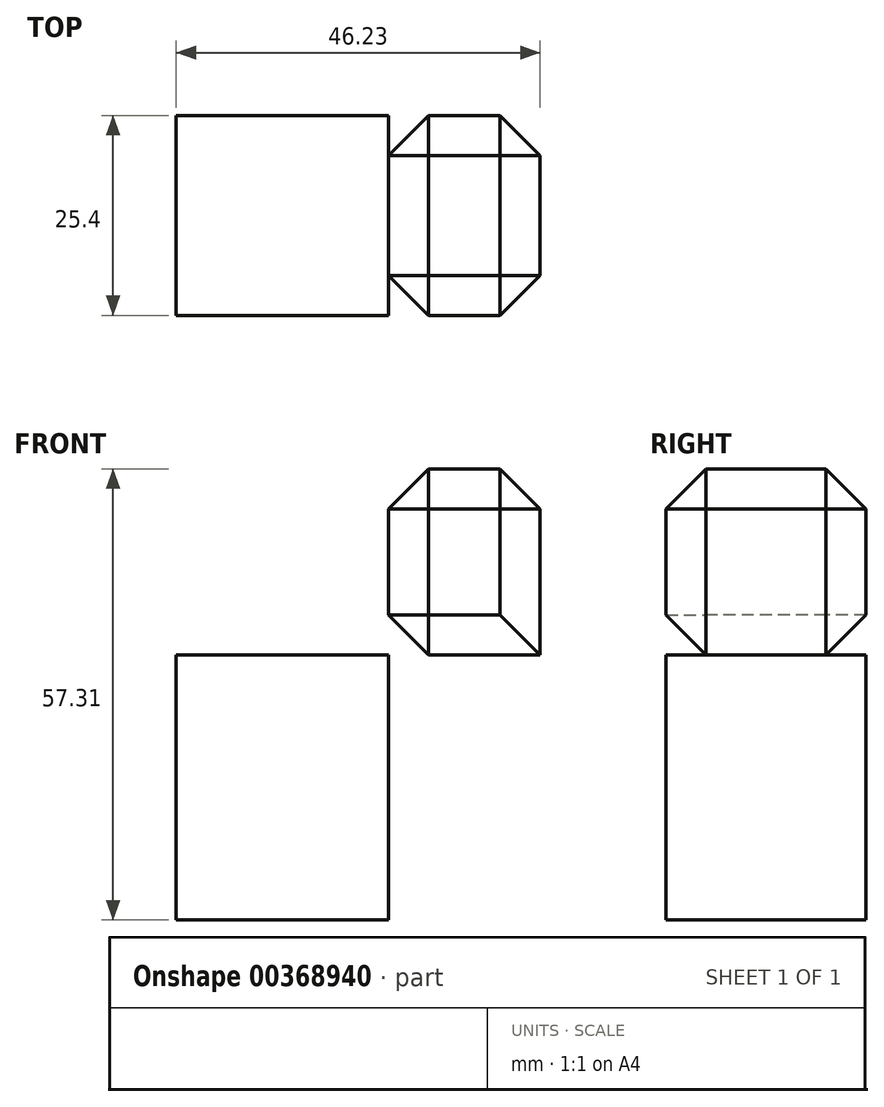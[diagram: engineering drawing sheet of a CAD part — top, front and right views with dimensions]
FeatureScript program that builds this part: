
annotation { "Feature Type Name" : "Feature", "Feature Type Description" : "" }
export const myFeature = defineFeature(function(context is Context, id is Id, definition is map)
    precondition{}
    {
        {
            var Q0;
            Q0=qCreatedBy(makeId("Front.planeOp"),FACE);
            var sketch = newSketch(context, id + "F0", { "sketchPlane" : qUnion([Q0])});
            skLineSegment(sketch, "E0.bottom", {"start": v(27.2, 31.48) * mm, "end": v(10.46, 31.48) * mm});
            skLineSegment(sketch, "E0.top", {"start": v(27.2, 12.24) * mm, "end": v(10.46, 12.24) * mm});
            skLineSegment(sketch, "E0.left", {"start": v(27.2, 31.48) * mm, "end": v(27.2, 12.24) * mm});
            skLineSegment(sketch, "E0.right", {"start": v(10.46, 31.48) * mm, "end": v(10.46, 12.24) * mm});
            skLineSegment(sketch, "E1.bottom", {"start": v(7.95, 7.84) * mm, "end": v(-19.04, 7.84) * mm});
            skLineSegment(sketch, "E1.top", {"start": v(7.95, -25.83) * mm, "end": v(-19.04, -25.83) * mm});
            skLineSegment(sketch, "E1.left", {"start": v(7.95, 7.84) * mm, "end": v(7.95, -25.83) * mm});
            skLineSegment(sketch, "E1.right", {"start": v(-19.04, 7.84) * mm, "end": v(-19.04, -25.83) * mm});
            skLineSegment(sketch, "E2.bottom", {"start": v(-19.04, -25.83) * mm, "end": v(7.95, -25.83) * mm});
            skLineSegment(sketch, "E2.top", {"start": v(-19.04, 7.84) * mm, "end": v(7.95, 7.84) * mm});
            skLineSegment(sketch, "E2.left", {"start": v(-19.04, -25.83) * mm, "end": v(-19.04, 7.84) * mm});
            skLineSegment(sketch, "E2.right", {"start": v(7.95, -25.83) * mm, "end": v(7.95, 7.84) * mm});
            skLineSegment(sketch, "E3.bottom", {"start": v(27.2, 31.48) * mm, "end": v(7.95, 31.48) * mm});
            skLineSegment(sketch, "E3.top", {"start": v(27.2, 7.84) * mm, "end": v(7.95, 7.84) * mm});
            skLineSegment(sketch, "E3.left", {"start": v(27.2, 31.48) * mm, "end": v(27.2, 7.84) * mm});
            skLineSegment(sketch, "E3.right", {"start": v(7.95, 31.48) * mm, "end": v(7.95, 7.84) * mm});
            skSolve(sketch);
        }
        {
            var Q0;
            Q0 = qSketchRegion(id + "F0", true);
            extrude(context, id + "F1", {"entities" : qUnion([Q0]), "depth" : 25.4 * mm});
        }
        {
            var Q0;
            Q0=makeQuery(id+"F1.opExtrude","CAP_EDGE",EDGE,{"disambiguationData":[OSD([sQuery(id+"F0.wireOp",EDGE,"E3.bottom")])],"isStart":true});
            var Q1;
            Q1=makeQuery(id+"F1.opExtrude","SWEPT_FACE",FACE,{"disambiguationData":[OSD([sQuery(id+"F0.wireOp",EDGE,"E3.bottom")])]});
            var Q2;
            Q2=makeQuery(id+"F1.opExtrude","CAP_FACE",FACE,{"disambiguationData":[OSD([sQuery(id+"F0.wireOp",EDGE,"E3.bottom"),sQuery(id+"F0.wireOp",EDGE,"E3.top"),sQuery(id+"F0.wireOp",EDGE,"E3.left"),sQuery(id+"F0.wireOp",EDGE,"E3.right")])],"isStart":true});
            var Q3;
            Q3=makeQuery(id+"F1.opExtrude","CAP_EDGE",EDGE,{"disambiguationData":[OSD([sQuery(id+"F0.wireOp",EDGE,"E3.right")])],"isStart":true});
            var Q4;
            Q4=makeQuery(id+"F1.opExtrude","CAP_EDGE",EDGE,{"disambiguationData":[OSD([sQuery(id+"F0.wireOp",EDGE,"E2.top")])],"isStart":true});
            var Q5;
            Q5=makeQuery(id+"F1.opExtrude","SWEPT_FACE",FACE,{"disambiguationData":[OSD([sQuery(id+"F0.wireOp",EDGE,"E2.left")])]});
            var Q6;
            Q6=makeQuery(id+"F1.opExtrude","CAP_FACE",FACE,{"disambiguationData":[OSD([sQuery(id+"F0.wireOp",EDGE,"E2.bottom"),sQuery(id+"F0.wireOp",EDGE,"E2.top"),sQuery(id+"F0.wireOp",EDGE,"E2.left"),sQuery(id+"F0.wireOp",EDGE,"E2.right")])],"isStart":true});
            var Q7;
            Q7=makeQuery(id+"F1.opExtrude","SWEPT_FACE",FACE,{"disambiguationData":[OSD([sQuery(id+"F0.wireOp",EDGE,"E3.right")])]});
            var Q8;
            Q8=makeQuery(id+"F1.opExtrude","SWEPT_EDGE",EDGE,{"disambiguationData":[OSD([sQuery(id+"F0.wireOp",EDGE,"E3.bottom"),sQuery(id+"F0.wireOp",EDGE,"E3.right")])]});
            var Q9;
            Q9=makeQuery(id+"F1.opExtrude","CAP_FACE",FACE,{"disambiguationData":[OSD([sQuery(id+"F0.wireOp",EDGE,"E3.bottom"),sQuery(id+"F0.wireOp",EDGE,"E3.top"),sQuery(id+"F0.wireOp",EDGE,"E3.left"),sQuery(id+"F0.wireOp",EDGE,"E3.right")])],"isStart":false});
            var Q10;
            Q10=makeQuery(id+"F1.opExtrude","CAP_EDGE",EDGE,{"disambiguationData":[OSD([sQuery(id+"F0.wireOp",EDGE,"E3.right")])],"isStart":false});
            var Q11;
            Q11=makeQuery(id+"F1.opExtrude","CAP_EDGE",EDGE,{"disambiguationData":[OSD([sQuery(id+"F0.wireOp",EDGE,"E2.top")])],"isStart":false});
            var Q12;
            Q12=makeQuery(id+"F1.opExtrude","CAP_EDGE",EDGE,{"disambiguationData":[OSD([sQuery(id+"F0.wireOp",EDGE,"E2.left")])],"isStart":false});
            var Q13;
            Q13=makeQuery(id+"F1.opExtrude","SWEPT_FACE",FACE,{"disambiguationData":[OSD([sQuery(id+"F0.wireOp",EDGE,"E2.top")])]});
            var Q14;
            Q14=makeQuery(id+"F1.opExtrude","CAP_FACE",FACE,{"disambiguationData":[OSD([sQuery(id+"F0.wireOp",EDGE,"E2.bottom"),sQuery(id+"F0.wireOp",EDGE,"E2.top"),sQuery(id+"F0.wireOp",EDGE,"E2.left"),sQuery(id+"F0.wireOp",EDGE,"E2.right")])],"isStart":false});
            var Q15;
            Q15=makeQuery(id+"F1.opExtrude","SWEPT_EDGE",EDGE,{"disambiguationData":[OSD([sQuery(id+"F0.wireOp",EDGE,"E2.top"),sQuery(id+"F0.wireOp",EDGE,"E2.left")])]});
            var Q16;
            Q16=makeQuery(id+"F1.opExtrude","CAP_EDGE",EDGE,{"disambiguationData":[OSD([sQuery(id+"F0.wireOp",EDGE,"E2.left")])],"isStart":true});
            var Q17;
            Q17=makeQuery(id+"F1.opExtrude","CAP_EDGE",EDGE,{"disambiguationData":[OSD([sQuery(id+"F0.wireOp",EDGE,"E2.bottom")])],"isStart":false});
            var Q18;
            Q18=makeQuery(id+"F1.opExtrude","SWEPT_EDGE",EDGE,{"disambiguationData":[OSD([sQuery(id+"F0.wireOp",EDGE,"E2.bottom"),sQuery(id+"F0.wireOp",EDGE,"E2.left")])]});
            var Q19;
            Q19=makeQuery(id+"F1.opExtrude","CAP_EDGE",EDGE,{"disambiguationData":[OSD([sQuery(id+"F0.wireOp",EDGE,"E2.right")])],"isStart":false});
            chamfer(context, id + "F2", {"entities" : qUnion([Q0, Q1, Q2, Q3, Q4, Q5, Q6, Q7, Q8, Q9, Q10, Q11, Q12, Q13, Q14, Q15, Q16, Q17, Q18, Q19]), "width" : 5.08 * mm, "tangentPropagation" : true});
        }
    });
